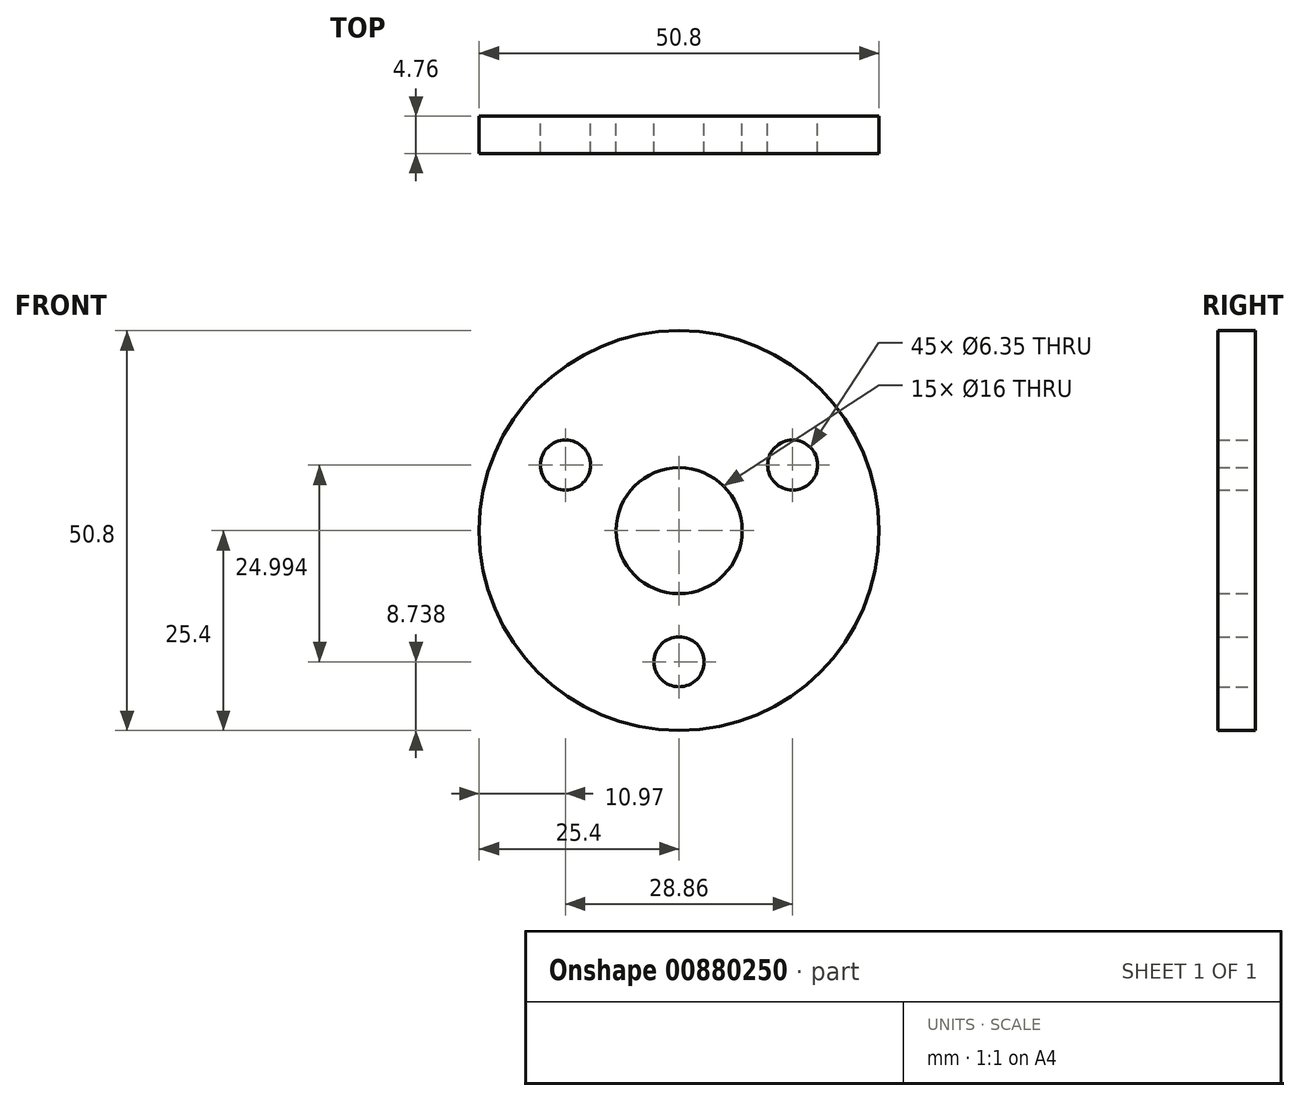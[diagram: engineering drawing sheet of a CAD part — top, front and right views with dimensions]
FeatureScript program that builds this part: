
annotation { "Feature Type Name" : "Feature", "Feature Type Description" : "" }
export const myFeature = defineFeature(function(context is Context, id is Id, definition is map)
    precondition{}
    {
        {
            var Q0;
            Q0=qCreatedBy(makeId("Front.planeOp"),FACE);
            var sketch = newSketch(context, id + "F0", { "sketchPlane" : qUnion([Q0])});
            skCircle(sketch, "E0", {"center": v(0, 0) * mm, "radius": 16.66 * mm, "construction": true});
            skCircle(sketch, "E1", {"center": v(-14.43, 8.33) * mm, "radius": 3.18 * mm});
            skCircle(sketch, "E2", {"center": v(14.43, 8.33) * mm, "radius": 3.18 * mm});
            skCircle(sketch, "E3", {"center": v(0, -16.66) * mm, "radius": 3.18 * mm});
            skCircle(sketch, "E4", {"center": v(0, 0) * mm, "radius": 25.4 * mm});
            skCircle(sketch, "E5", {"center": v(0, 0) * mm, "radius": 8 * mm});
            skLineSegment(sketch, "E6", {"start": v(-14.43, 8.33) * mm, "end": v(0, -16.66) * mm, "construction": true});
            skLineSegment(sketch, "E7", {"start": v(14.43, 8.33) * mm, "end": v(0, -16.66) * mm, "construction": true});
            skLineSegment(sketch, "E8", {"start": v(14.43, 8.33) * mm, "end": v(-14.43, 8.33) * mm, "construction": true});
            skSolve(sketch);
        }
        {
            var Q0;
            Q0=qSketchRegion(id+"F0",true);
            extrude(context, id + "F1", {"entities" : qUnion([Q0]), "depth" : 4.76 * mm});
        }
    });
